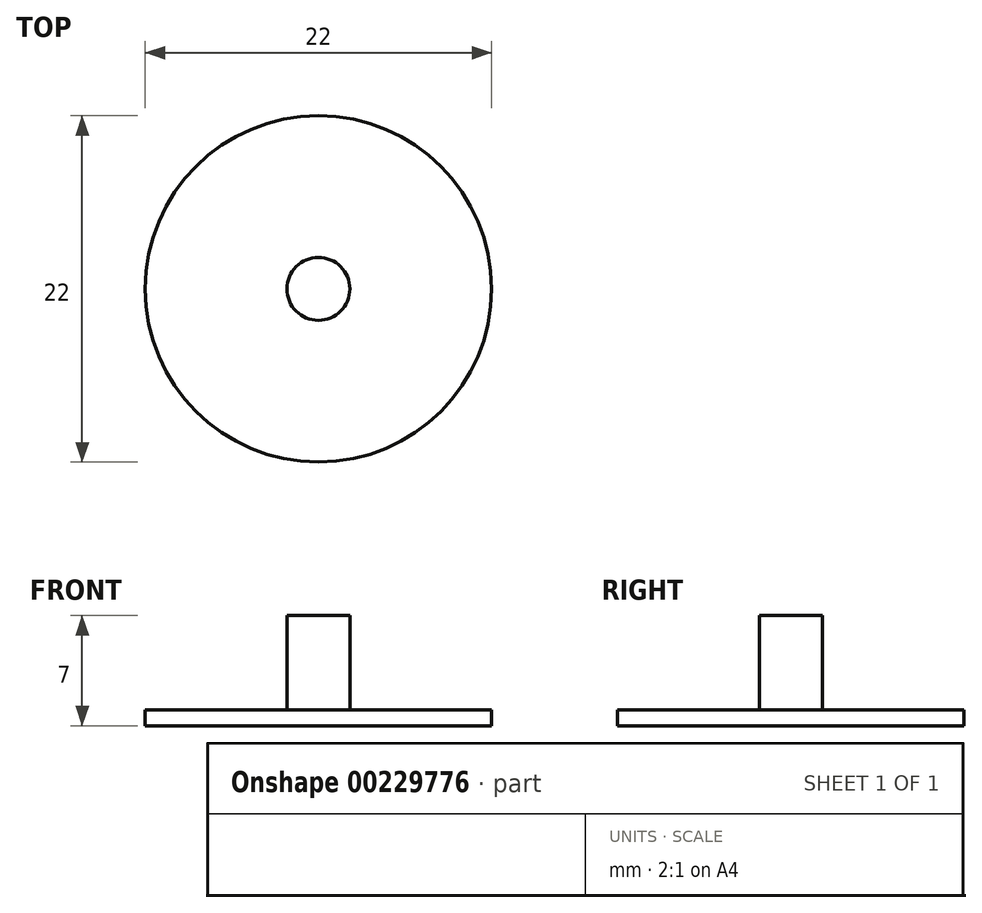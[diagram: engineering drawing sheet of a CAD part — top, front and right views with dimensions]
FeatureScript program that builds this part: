
annotation { "Feature Type Name" : "Feature", "Feature Type Description" : "" }
export const myFeature = defineFeature(function(context is Context, id is Id, definition is map)
    precondition{}
    {
        {
            var Q0;
            Q0=qCreatedBy(makeId("Top.planeOp"),FACE);
            var sketch = newSketch(context, id + "F0", { "sketchPlane" : qUnion([Q0])});
            skCircle(sketch, "E0", {"center": v(0, 0) * mm, "radius": 11 * mm});
            skCircle(sketch, "E1", {"center": v(0, 0) * mm, "radius": 2 * mm});
            skSolve(sketch);
        }
        {
            var Q0;
            Q0=makeQuery(id+"F0.imprint","IMPRINT",FACE,{"disambiguationData":[TD([[makeQuery(id+"F0.imprint","IMPRINT",EDGE,{"derivedFrom":sQuery(id+"F0.wireOp",EDGE,"E0")}),1.0]])]});
            var Q1;
            Q1=makeQuery(id+"F0.imprint","IMPRINT",FACE,{"disambiguationData":[TD([[makeQuery(id+"F0.imprint","IMPRINT",EDGE,{"derivedFrom":sQuery(id+"F0.wireOp",EDGE,"E1")}),1.0]])]});
            extrude(context, id + "F1", {"entities" : qUnion([Q0, Q1]), "depth" : 1 * mm, "offsetDistance" : 25.4 * mm});
        }
        {
            var Q0;
            Q0=makeQuery(id+"F1.opExtrude","CAP_FACE",FACE,{"disambiguationData":[OSD([sQuery(id+"F0.wireOp",EDGE,"E0")])],"isStart":false});
            var sketch = newSketch(context, id + "F2", { "sketchPlane" : qUnion([Q0])});
            skCircle(sketch, "E2", {"center": v(0, 0) * mm, "radius": 2 * mm});
            skSolve(sketch);
        }
        {
            var Q0;
            Q0 = qSketchRegion(id + "F2", true);
            extrude(context, id + "F3", {"entities" : qUnion([Q0]), "operationType" : NewBodyOperationType.ADD, "depth" : 6 * mm, "offsetDistance" : 25.4 * mm});
        }
    });
